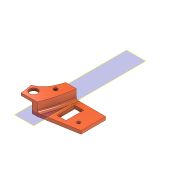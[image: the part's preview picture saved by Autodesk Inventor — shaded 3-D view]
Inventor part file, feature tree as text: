
AUTODESK INVENTOR PART (.ipt)
format: ipt  version: 2020.3 (Build 243373000, 373)  size: 296,960 bytes
history: native  units: mm
features: extrude x5, sketch x3, fillet x2, plane x1
ambient origin geometry x8: Origin, YZ Plane, XZ Plane, XY Plane, X Axis, Y Axis, Z Axis, Center Point
bodies: Solid1 (feature_tree)
feature tree (11):
  sketch  "Sketch1"  dims[d1=40.0mm d3=20.0mm d5=200.0mm d6=60.0mm d7=81.0mm d8=3.0mm d9=7.5mm d10=5.0mm d11=30.0mm d12=3.0mm d13=7.5mm d14=5.0mm d15=3.0mm d16=3.0mm d17=5.0mm d18=48.0mm d19=55.0mm d20=3.0mm d21=4.5mm d22=3.0mm d23=4.5mm d24=360.0deg d25=80.0mm d26=72.56mm d27=3.0mm d28=3.0mm d29=360.0deg d30=45.0deg d31=3.0mm d32=360.0deg d33=3.0mm d34=3.0mm d35=3.0mm d36=3.0mm d37=6.0mm]
  extrude  "Extrusion1"  Depth=6.0mm
  extrude  "Extrusion2"  Depth=30.0mm
  plane  "Work Plane1"
  sketch  "Sketch2"  dims[d38=5.0mm d39=30.0mm]
  extrude  "Extrusion3"  Depth=2.5mm
  extrude  "Extrusion4"  Depth=10.0mm
  fillet  "Fillet1"  Radius=19.0mm
  fillet  "Fillet2"  Radius=14.0mm
  extrude  "Extrusion5"  Depth=2.5mm
  sketch  "Sketch3"  dims[d40=40.5mm d41=13.0mm d42=10.0mm d43=19.0mm d44=14.0mm d45=7.0mm d46=2.0mm d47=2.0mm d48=2.0mm d49=2.0mm d50=2.0mm d51=2.0mm d52=7.0mm d53=2.5mm d54=2.5mm d55=1.6mm d56=1.6mm d57=2.5mm d58=2.0mm d59=2.0mm d60=35.0mm d61=16.0mm d62=4.0mm d63=6.0mm d64=22.0mm d65=14.0mm d66=13.962634mm d67=13.962634mm d68=2.0mm d69=4.0mm d70=2.0mm d71=0.0mm d72=4.0mm d73=0.0mm d74=1.5mm d75=2.5mm d76=0.0mm d77=2.0mm d78=6.5mm d79=6.5mm d80=1.25mm d81=0.0mm d82=15.0mm d83=1.6mm d84=15.75mm d85=0.0mm]
